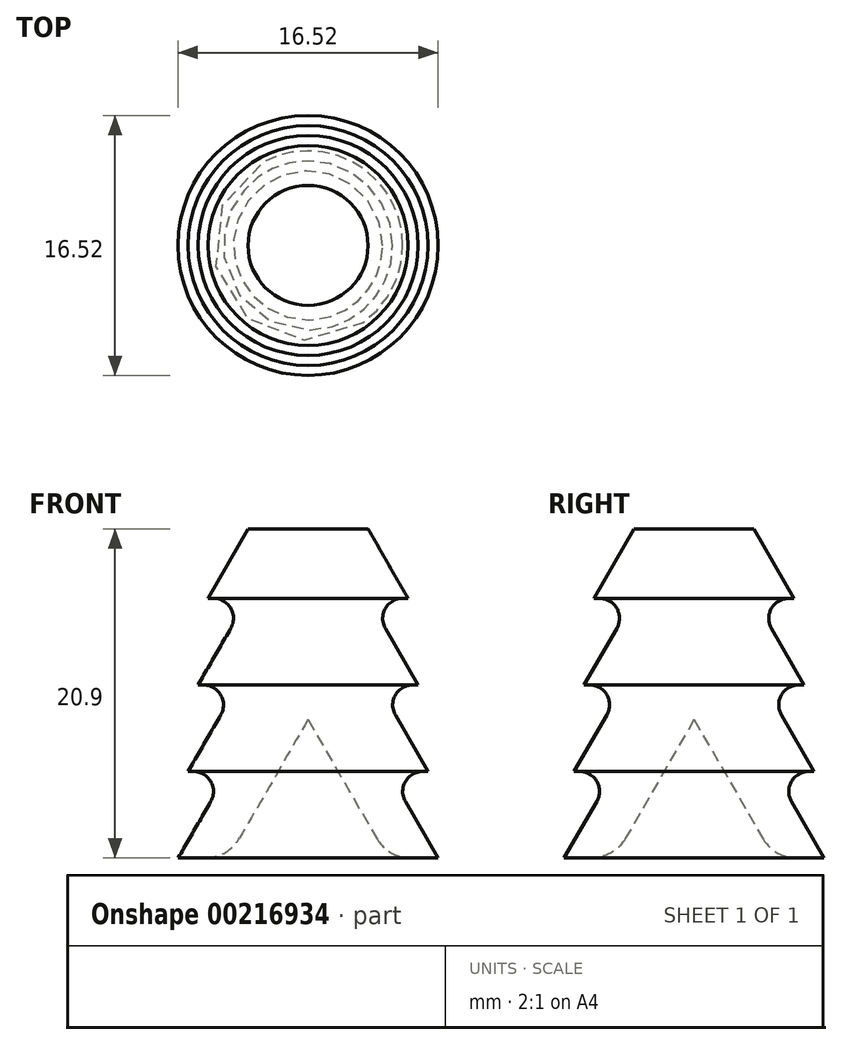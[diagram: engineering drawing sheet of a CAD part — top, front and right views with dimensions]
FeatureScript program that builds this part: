
annotation { "Feature Type Name" : "Feature", "Feature Type Description" : "" }
export const myFeature = defineFeature(function(context is Context, id is Id, definition is map)
    precondition{}
    {
        {
            var Q0;
            Q0=qCreatedBy(makeId("Front.planeOp"),FACE);
            var sketch = newSketch(context, id + "F0", { "sketchPlane" : qUnion([Q0])});
            skLineSegment(sketch, "E0", {"start": v(8.26, 0) * mm, "end": v(5.08, 5.5) * mm});
            skLineSegment(sketch, "E1", {"start": v(5.08, 5.5) * mm, "end": v(7.62, 5.5) * mm});
            skLineSegment(sketch, "E2", {"start": v(7.62, 5.5) * mm, "end": v(4.45, 11) * mm});
            skLineSegment(sketch, "E3", {"start": v(4.45, 11) * mm, "end": v(6.99, 11) * mm});
            skLineSegment(sketch, "E4", {"start": v(6.99, 11) * mm, "end": v(3.81, 16.5) * mm});
            skLineSegment(sketch, "E5", {"start": v(3.81, 16.5) * mm, "end": v(6.35, 16.5) * mm});
            skLineSegment(sketch, "E6", {"start": v(6.35, 16.5) * mm, "end": v(3.81, 20.9) * mm});
            skLineSegment(sketch, "E7", {"start": v(3.8, 20.9) * mm, "end": v(0, 20.9) * mm});
            skLineSegment(sketch, "E8", {"start": v(3.81, 16.5) * mm, "end": v(3.8, 20.9) * mm, "construction": true});
            skLineSegment(sketch, "E9", {"start": v(8.26, 0) * mm, "end": v(5.08, 0) * mm});
            skLineSegment(sketch, "E10", {"start": v(5.08, 0) * mm, "end": v(5.08, 5.5) * mm, "construction": true});
            skLineSegment(sketch, "E11", {"start": v(5.08, 0) * mm, "end": v(0, 8.8) * mm});
            skLineSegment(sketch, "E12", {"start": v(0, 20.9) * mm, "end": v(0, 8.8) * mm});
            skSolve(sketch);
        }
        {
            var Q0;
            Q0=makeQuery(id+"F0.imprint","IMPRINT",FACE,{"disambiguationData":[TD([[makeQuery(id+"F0.imprint","IMPRINT",EDGE,{"derivedFrom":sQuery(id+"F0.wireOp",EDGE,"E0")}),1.0]])]});
            var Q1;
            Q1=sQuery(id+"F0.wireOp",EDGE,"E12");
            revolve(context, id + "F1", {"entities" : qUnion([Q0]), "axis" : qUnion([Q1]), "revolveType" : RevolveType.FULL});
        }
        {
            var Q0;
            Q0=makeQuery(id+"F1.opRevolve","SWEPT_EDGE",EDGE,{"disambiguationData":[OSD([sQuery(id+"F0.wireOp",EDGE,"E9"),sQuery(id+"F0.wireOp",EDGE,"E11")])]});
            fillet(context, id + "F2", {"entities" : qUnion([Q0]), "radius" : 2.54 * mm, "tangentPropagation" : true, "allowEdgeOverflow" : false});
        }
        {
            var Q0;
            Q0=makeQuery(id+"F1.opRevolve","SWEPT_EDGE",EDGE,{"disambiguationData":[OSD([sQuery(id+"F0.wireOp",EDGE,"E0"),sQuery(id+"F0.wireOp",EDGE,"E1")])]});
            var Q1;
            Q1=makeQuery(id+"F1.opRevolve","SWEPT_EDGE",EDGE,{"disambiguationData":[OSD([sQuery(id+"F0.wireOp",EDGE,"E2"),sQuery(id+"F0.wireOp",EDGE,"E3")])]});
            var Q2;
            Q2=makeQuery(id+"F1.opRevolve","SWEPT_EDGE",EDGE,{"disambiguationData":[OSD([sQuery(id+"F0.wireOp",EDGE,"E4"),sQuery(id+"F0.wireOp",EDGE,"E5")])]});
            fillet(context, id + "F3", {"entities" : qUnion([Q0, Q1, Q2]), "radius" : 1.27 * mm, "tangentPropagation" : true, "allowEdgeOverflow" : false});
        }
    });
